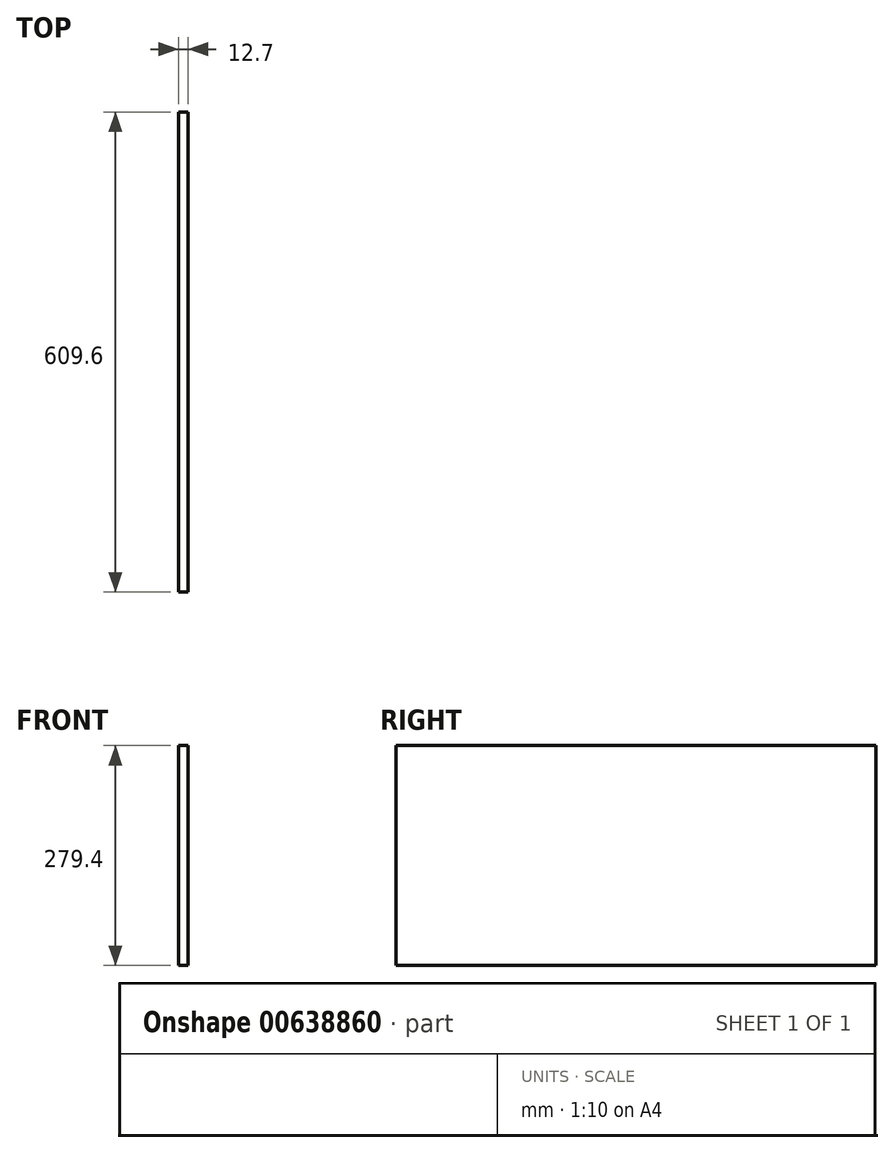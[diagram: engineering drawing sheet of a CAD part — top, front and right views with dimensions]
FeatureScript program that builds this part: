
annotation { "Feature Type Name" : "Feature", "Feature Type Description" : "" }
export const myFeature = defineFeature(function(context is Context, id is Id, definition is map)
    precondition{}
    {
        {
            var Q0;
            Q0=qCreatedBy(makeId("Right.planeOp"),FACE);
            var sketch = newSketch(context, id + "F0", { "sketchPlane" : qUnion([Q0])});
            skLineSegment(sketch, "E0.bottom", {"start": v(304.8, 139.7) * mm, "end": v(-304.8, 139.7) * mm});
            skLineSegment(sketch, "E0.top", {"start": v(304.8, -139.7) * mm, "end": v(-304.8, -139.7) * mm});
            skLineSegment(sketch, "E0.left", {"start": v(304.8, 139.7) * mm, "end": v(304.8, -139.7) * mm});
            skLineSegment(sketch, "E0.right", {"start": v(-304.8, 139.7) * mm, "end": v(-304.8, -139.7) * mm});
            skPoint(sketch, "E0.middle", {"position": v(0, 0) * mm});
            skSolve(sketch);
        }
        {
            var Q0;
            Q0=makeQuery(id+"F0.imprint","IMPRINT",FACE,{"disambiguationData":[TD([[makeQuery(id+"F0.imprint","IMPRINT",EDGE,{"derivedFrom":sQuery(id+"F0.wireOp",EDGE,"E0.bottom")}),1.0]])]});
            extrude(context, id + "F1", {"entities" : qUnion([Q0]), "depth" : 12.7 * mm, "offsetDistance" : 25.4 * mm});
        }
    });
